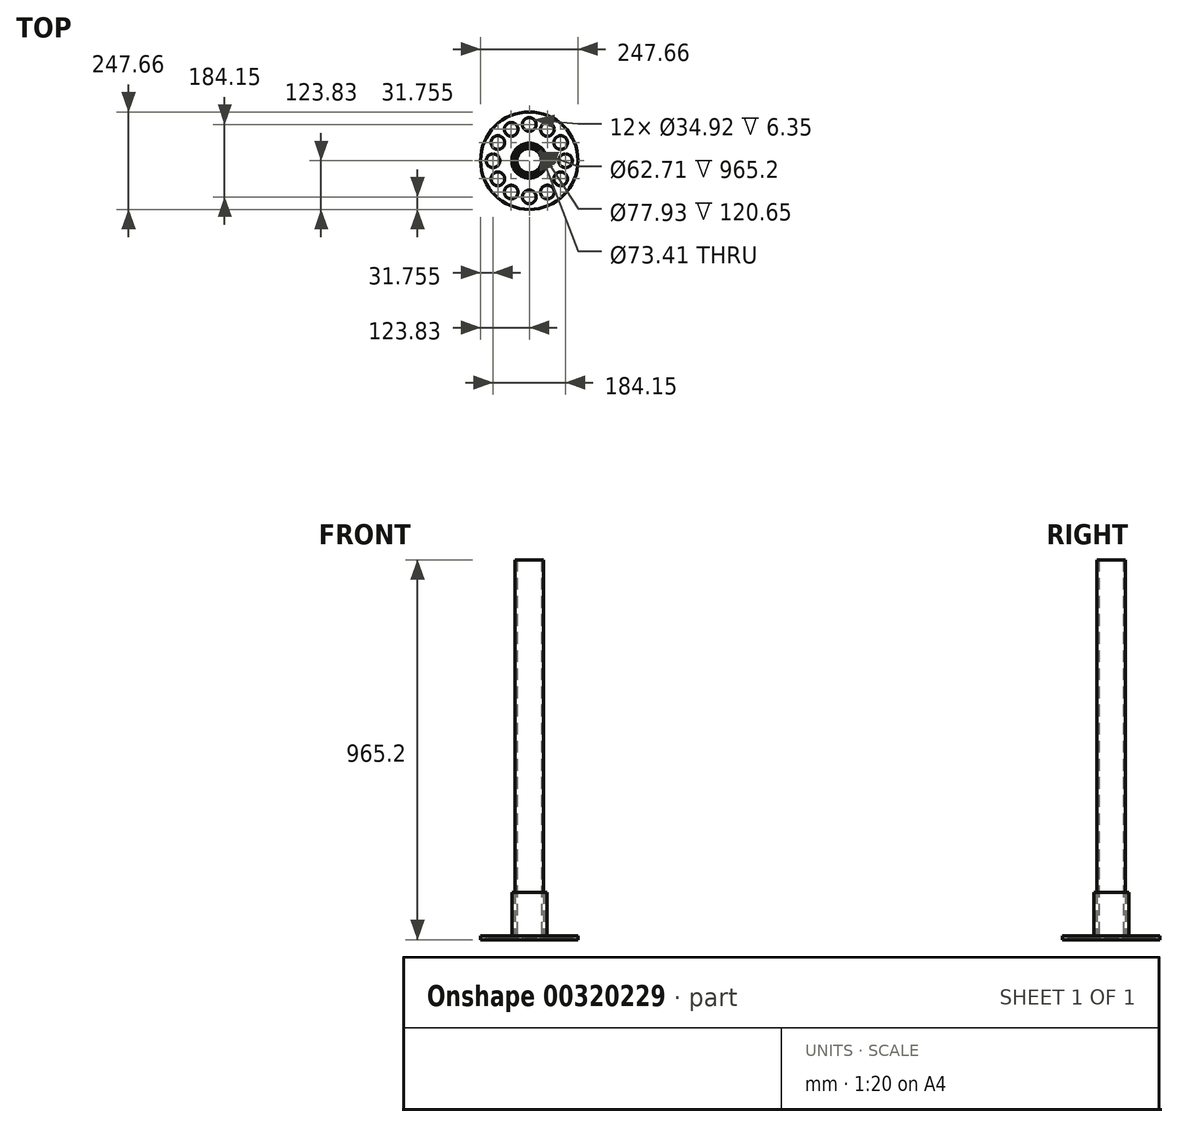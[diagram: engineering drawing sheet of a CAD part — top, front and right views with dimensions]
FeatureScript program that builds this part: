
annotation { "Feature Type Name" : "Feature", "Feature Type Description" : "" }
export const myFeature = defineFeature(function(context is Context, id is Id, definition is map)
    precondition{}
    {
        {
            var Q0;
            Q0=qCreatedBy(makeId("Top.planeOp"),FACE);
            var sketch = newSketch(context, id + "F0", { "sketchPlane" : qUnion([Q0])});
            skCircle(sketch, "E0.cCircle", {"center": v(0, 0) * mm, "radius": 92.08 * mm, "construction": true});
            skLineSegment(sketch, "E0.0", {"start": v(-92.07, 0) * mm, "end": v(-79.74, 46.04) * mm, "construction": true});
            skLineSegment(sketch, "E0.1", {"start": v(-79.74, 46.04) * mm, "end": v(-46.04, 79.74) * mm, "construction": true});
            skLineSegment(sketch, "E0.2", {"start": v(-46.04, 79.74) * mm, "end": v(0, 92.08) * mm, "construction": true});
            skLineSegment(sketch, "E0.3", {"start": v(0, 92.07) * mm, "end": v(46.04, 79.74) * mm, "construction": true});
            skLineSegment(sketch, "E0.4", {"start": v(46.04, 79.74) * mm, "end": v(79.74, 46.04) * mm, "construction": true});
            skLineSegment(sketch, "E0.5", {"start": v(79.74, 46.04) * mm, "end": v(92.08, 0) * mm, "construction": true});
            skLineSegment(sketch, "E0.6", {"start": v(92.07, 0) * mm, "end": v(79.74, -46.04) * mm, "construction": true});
            skLineSegment(sketch, "E0.7", {"start": v(79.74, -46.04) * mm, "end": v(46.04, -79.74) * mm, "construction": true});
            skLineSegment(sketch, "E0.8", {"start": v(46.04, -79.74) * mm, "end": v(0, -92.08) * mm, "construction": true});
            skLineSegment(sketch, "E0.9", {"start": v(0, -92.07) * mm, "end": v(-46.04, -79.74) * mm, "construction": true});
            skLineSegment(sketch, "E0.10", {"start": v(-46.04, -79.74) * mm, "end": v(-79.74, -46.04) * mm, "construction": true});
            skLineSegment(sketch, "E0.11", {"start": v(-79.74, -46.04) * mm, "end": v(-92.08, 0) * mm, "construction": true});
            skCircle(sketch, "E1", {"center": v(0, 0) * mm, "radius": 123.83 * mm});
            skCircle(sketch, "E2", {"center": v(-92.07, 0) * mm, "radius": 17.46 * mm});
            skCircle(sketch, "E3.1.0", {"center": v(-79.74, 46.04) * mm, "radius": 17.46 * mm});
            skCircle(sketch, "E3.2.0", {"center": v(-46.04, 79.74) * mm, "radius": 17.46 * mm});
            skCircle(sketch, "E3.3.0", {"center": v(0, 92.08) * mm, "radius": 17.46 * mm});
            skCircle(sketch, "E3.4.0", {"center": v(46.04, 79.74) * mm, "radius": 17.46 * mm});
            skCircle(sketch, "E3.5.0", {"center": v(79.74, 46.04) * mm, "radius": 17.46 * mm});
            skCircle(sketch, "E3.6.0", {"center": v(92.08, 0) * mm, "radius": 17.46 * mm});
            skCircle(sketch, "E3.7.0", {"center": v(79.74, -46.04) * mm, "radius": 17.46 * mm});
            skCircle(sketch, "E3.8.0", {"center": v(46.04, -79.74) * mm, "radius": 17.46 * mm});
            skCircle(sketch, "E3.9.0", {"center": v(0, -92.08) * mm, "radius": 17.46 * mm});
            skCircle(sketch, "E3.10.0", {"center": v(-46.04, -79.74) * mm, "radius": 17.46 * mm});
            skCircle(sketch, "E3.11.0", {"center": v(-79.74, -46.04) * mm, "radius": 17.46 * mm});
            skLineSegment(sketch, "E3.anchor1", {"start": v(0, 0) * mm, "end": v(-92.08, 0) * mm, "construction": true});
            skLineSegment(sketch, "E3.anchor2", {"start": v(0, 0) * mm, "end": v(-79.74, -46.04) * mm, "construction": true});
            skCircle(sketch, "E4", {"center": v(0, 0) * mm, "radius": 36.7 * mm});
            skCircle(sketch, "E5", {"center": v(0, 0) * mm, "radius": 36.51 * mm});
            skCircle(sketch, "E6", {"center": v(0, 0) * mm, "radius": 31.36 * mm});
            skCircle(sketch, "E7", {"center": v(0, 0) * mm, "radius": 44.45 * mm});
            skCircle(sketch, "E8", {"center": v(0, 0) * mm, "radius": 38.96 * mm});
            skSolve(sketch);
        }
        {
            var Q0;
            Q0=makeQuery(id+"F0.imprint","IMPRINT",FACE,{"disambiguationData":[TD([[makeQuery(id+"F0.imprint","IMPRINT",EDGE,{"derivedFrom":sQuery(id+"F0.wireOp",EDGE,"E1")}),1.0]])]});
            var Q1;
            Q1=makeQuery(id+"F0.imprint","IMPRINT",FACE,{"disambiguationData":[TD([[makeQuery(id+"F0.imprint","IMPRINT",EDGE,{"derivedFrom":sQuery(id+"F0.wireOp",EDGE,"E4")}),-1.0]])]});
            var Q2;
            Q2=makeQuery(id+"F0.imprint","IMPRINT",FACE,{"disambiguationData":[TD([[makeQuery(id+"F0.imprint","IMPRINT",EDGE,{"derivedFrom":sQuery(id+"F0.wireOp",EDGE,"E7")}),1.0]])]});
            extrude(context, id + "F1", {"entities" : qUnion([Q0, Q1, Q2]), "depth" : 9.52 * mm, "offsetDistance" : 25.4 * mm});
        }
        {
            var Q0;
            Q0=makeQuery(id+"F0.imprint","IMPRINT",FACE,{"disambiguationData":[TD([[makeQuery(id+"F0.imprint","IMPRINT",EDGE,{"derivedFrom":sQuery(id+"F0.wireOp",EDGE,"E3.2.0")}),1.0]])]});
            var Q1;
            Q1=makeQuery(id+"F0.imprint","IMPRINT",FACE,{"disambiguationData":[TD([[makeQuery(id+"F0.imprint","IMPRINT",EDGE,{"derivedFrom":sQuery(id+"F0.wireOp",EDGE,"E3.3.0")}),1.0]])]});
            var Q2;
            Q2=makeQuery(id+"F0.imprint","IMPRINT",FACE,{"disambiguationData":[TD([[makeQuery(id+"F0.imprint","IMPRINT",EDGE,{"derivedFrom":sQuery(id+"F0.wireOp",EDGE,"E3.4.0")}),1.0]])]});
            var Q3;
            Q3=makeQuery(id+"F0.imprint","IMPRINT",FACE,{"disambiguationData":[TD([[makeQuery(id+"F0.imprint","IMPRINT",EDGE,{"derivedFrom":sQuery(id+"F0.wireOp",EDGE,"E3.6.0")}),1.0]])]});
            var Q4;
            Q4=makeQuery(id+"F0.imprint","IMPRINT",FACE,{"disambiguationData":[TD([[makeQuery(id+"F0.imprint","IMPRINT",EDGE,{"derivedFrom":sQuery(id+"F0.wireOp",EDGE,"E3.5.0")}),1.0]])]});
            var Q5;
            Q5=makeQuery(id+"F0.imprint","IMPRINT",FACE,{"disambiguationData":[TD([[makeQuery(id+"F0.imprint","IMPRINT",EDGE,{"derivedFrom":sQuery(id+"F0.wireOp",EDGE,"E3.7.0")}),1.0]])]});
            var Q6;
            Q6=makeQuery(id+"F0.imprint","IMPRINT",FACE,{"disambiguationData":[TD([[makeQuery(id+"F0.imprint","IMPRINT",EDGE,{"derivedFrom":sQuery(id+"F0.wireOp",EDGE,"E3.8.0")}),1.0]])]});
            var Q7;
            Q7=makeQuery(id+"F0.imprint","IMPRINT",FACE,{"disambiguationData":[TD([[makeQuery(id+"F0.imprint","IMPRINT",EDGE,{"derivedFrom":sQuery(id+"F0.wireOp",EDGE,"E3.9.0")}),1.0]])]});
            var Q8;
            Q8=makeQuery(id+"F0.imprint","IMPRINT",FACE,{"disambiguationData":[TD([[makeQuery(id+"F0.imprint","IMPRINT",EDGE,{"derivedFrom":sQuery(id+"F0.wireOp",EDGE,"E3.10.0")}),1.0]])]});
            var Q9;
            Q9=makeQuery(id+"F0.imprint","IMPRINT",FACE,{"disambiguationData":[TD([[makeQuery(id+"F0.imprint","IMPRINT",EDGE,{"derivedFrom":sQuery(id+"F0.wireOp",EDGE,"E3.11.0")}),1.0]])]});
            var Q10;
            Q10=makeQuery(id+"F0.imprint","IMPRINT",FACE,{"disambiguationData":[TD([[makeQuery(id+"F0.imprint","IMPRINT",EDGE,{"derivedFrom":sQuery(id+"F0.wireOp",EDGE,"E2")}),1.0]])]});
            var Q11;
            Q11=makeQuery(id+"F0.imprint","IMPRINT",FACE,{"disambiguationData":[TD([[makeQuery(id+"F0.imprint","IMPRINT",EDGE,{"derivedFrom":sQuery(id+"F0.wireOp",EDGE,"E3.1.0")}),1.0]])]});
            extrude(context, id + "F2", {"entities" : qUnion([Q0, Q1, Q2, Q3, Q4, Q5, Q6, Q7, Q8, Q9, Q10, Q11]), "operationType" : NewBodyOperationType.ADD, "depth" : 3.17 * mm, "offsetDistance" : 25.4 * mm});
        }
        {
            var Q0;
            Q0=makeQuery(id+"F0.imprint","IMPRINT",FACE,{"disambiguationData":[TD([[makeQuery(id+"F0.imprint","IMPRINT",EDGE,{"derivedFrom":sQuery(id+"F0.wireOp",EDGE,"E5")}),1.0]])]});
            extrude(context, id + "F3", {"entities" : qUnion([Q0]), "depth" : 965.2 * mm, "offsetDistance" : 25.4 * mm});
        }
        {
            var Q0;
            Q0=makeQuery(id+"F0.imprint","IMPRINT",FACE,{"disambiguationData":[TD([[makeQuery(id+"F0.imprint","IMPRINT",EDGE,{"derivedFrom":sQuery(id+"F0.wireOp",EDGE,"E7")}),1.0]])]});
            extrude(context, id + "F4", {"entities" : qUnion([Q0]), "depth" : 120.65 * mm, "offsetDistance" : 25.4 * mm});
        }
    });
